# Revit family: SUBLIME RF_0750
name_source: partatom
category: Generic Models
revit_build: Autodesk Revit 2018 (Build: 20190510_1515(x64)
units: mm (PartAtom-declared; Revit-internal decimal feet)

## family parameters
Always vertical = Yes
Can host rebar = No
Cut with Voids When Loaded = No
Part Type = Normal
Room Calculation Point = No
Round Connector Dimension = Use Diameter
Shared = No
Work Plane-Based = No

## types (15) — shared parameters
Diepte = 80 mm  [stored 0.262467 ft]
H openingen = 488 mm
H openingen o = 478 mm  [stored 1.56824 ft]
Hoogte = 500 mm  [stored 1.64042 ft]
Kleur = Lacquer White
Licht grijs = Licht grijs
Manufacturer = Masterwatt B.V.
Phase = 1
Scherm = Screen
URL = https://masterwatt.nl
Voltage = 230 V
Zwart = Zwart

## per-type parameters (varying)
| type | Aantal openingen boven | Aantal openingen onder | Art. No. | Beugel breed | Beugel smal | Breedte | Model | Plus paneel | Power (default) | RF model | Wifi paneel |
| Sublime plus_0750 | 35 | 24 | 429 756 311 | No | Yes | 750 mm  [stored 2.46063 ft] | SBL 750 PLUS | Yes | 750 VA | No | No |
| Sublime plus_1500 | 50 | 39 | 429 756 314 | Yes | No | 1050 mm | SBL 1500 PLUS | Yes | 1500 VA | No | No |
| Sublime plus_1000 | 35 | 24 | 429 756 312 | No | Yes | 750 mm  [stored 2.46063 ft] | SBL 1000 PLUS | Yes | 1000 VA | No | No |
| Sublime plus_1200 | 35 | 24 | 429 756 313 | No | Yes | 750 mm  [stored 2.46063 ft] | SBL 1200 PLUS | Yes | 1200 VA | No | No |
| Sublime plus_2000 | 50 | 39 | 429 756 315 | Yes | No | 1050 mm | SBL 2000 PLUS | Yes | 2000 VA | No | No |
| Sublime RF_2000 | 50 | 39 | 429 756 325 | Yes | No | 1050 mm | SBL 2000 RF | No | 2000 VA | Yes | No |
| Sublime RF_0750 | 35 | 24 | 429 756 321 | No | Yes | 750 mm  [stored 2.46063 ft] | SBL 750 RF | No | 750 VA | Yes | No |
| Sublime RF_1000 | 35 | 24 | 429 756 322 | No | Yes | 750 mm  [stored 2.46063 ft] | SBL 1000 RF | No | 1000 VA | Yes | No |
| Sublime RF_1200 | 35 | 24 | 429 756 323 | No | Yes | 750 mm  [stored 2.46063 ft] | SBL 1200 RF | No | 1200 VA | Yes | No |
| Sublime RF_1500 | 50 | 39 | 429 756 324 | Yes | No | 1050 mm | SBL 1500 RF | No | 1500 VA | Yes | No |
| Sublime Wifi_2000 | 50 | 39 | 429 756 335 | Yes | No | 1050 mm | SBL 2000 WIFI | No | 2000 VA | No | Yes |
| Sublime Wifi_1500 | 50 | 39 | 429 756 334 | Yes | No | 1050 mm | SBL 1500 WIFI | No | 1500 VA | No | Yes |
| Sublime Wifi_1200 | 35 | 24 | 429 756 333 | No | Yes | 750 mm  [stored 2.46063 ft] | SBL 1200 Wifi | No | 1200 VA | No | Yes |
| Sublime Wifi_1000 | 35 | 24 | 429 756 332 | No | Yes | 750 mm  [stored 2.46063 ft] | SBL 1000 Wifi | No | 1000 VA | No | Yes |
| Sublime Wifi_0750 | 35 | 24 | 429 756 331 | No | Yes | 750 mm  [stored 2.46063 ft] | SBL 750 Wifi | No | 750 VA | No | Yes |

note: [stored X ft] marks values corroborated as IEEE doubles in the binary element streams (Revit-internal decimal feet)

## geometry (parser evidence)
native form markers: Sweep x23
no freeform markers — native parametric forms only
